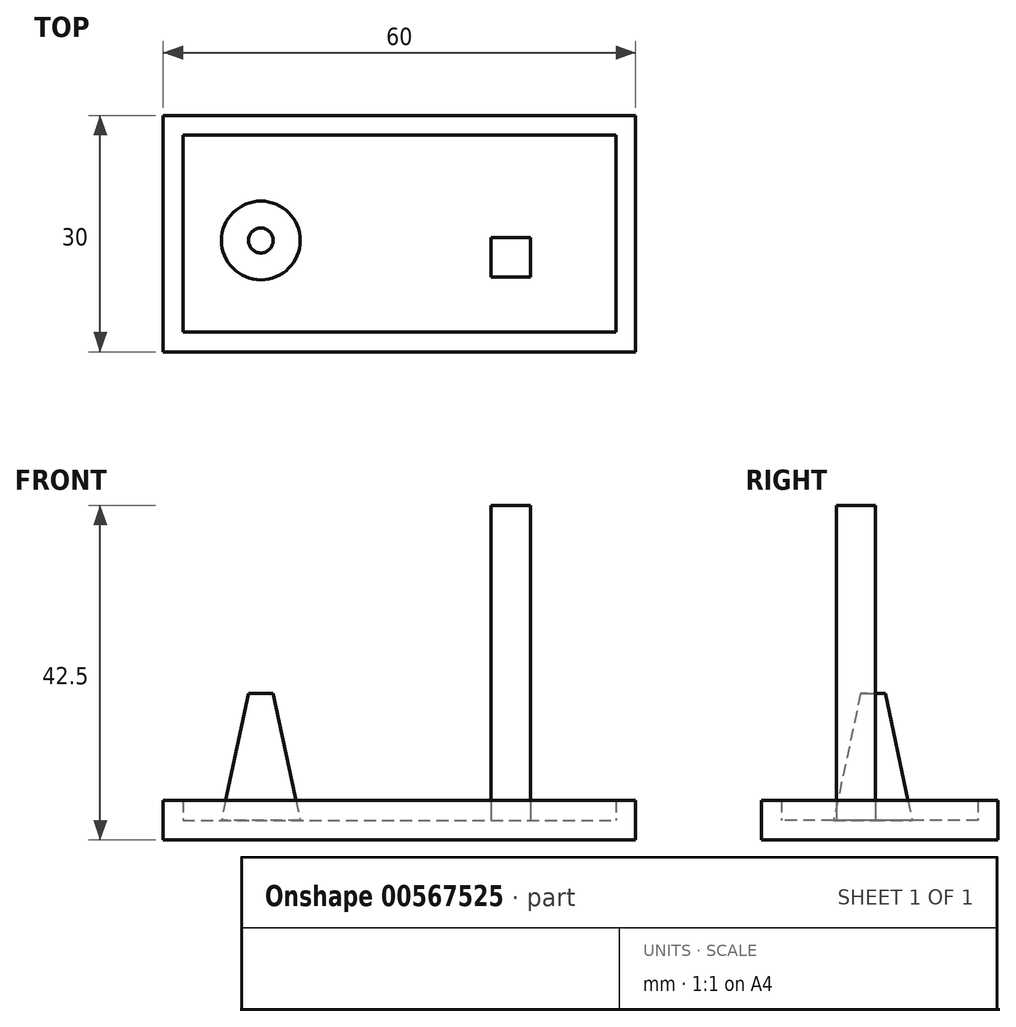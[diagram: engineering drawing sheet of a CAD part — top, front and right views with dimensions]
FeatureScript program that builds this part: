
annotation { "Feature Type Name" : "Feature", "Feature Type Description" : "" }
export const myFeature = defineFeature(function(context is Context, id is Id, definition is map)
    precondition{}
    {
        {
            var Q0;
            Q0=qCreatedBy(makeId("Top.planeOp"),FACE);
            var sketch = newSketch(context, id + "F0", { "sketchPlane" : qUnion([Q0])});
            skLineSegment(sketch, "E0.bottom", {"start": v(-26.67, 19.74) * mm, "end": v(33.33, 19.74) * mm});
            skLineSegment(sketch, "E0.top", {"start": v(-26.67, -10.26) * mm, "end": v(33.33, -10.26) * mm});
            skLineSegment(sketch, "E0.left", {"start": v(-26.67, 19.74) * mm, "end": v(-26.67, -10.26) * mm});
            skLineSegment(sketch, "E0.right", {"start": v(33.33, 19.74) * mm, "end": v(33.33, -10.26) * mm});
            skSolve(sketch);
        }
        {
            var Q0;
            Q0=makeQuery(id+"F0.imprint","IMPRINT",FACE,{"disambiguationData":[TD([[makeQuery(id+"F0.imprint","IMPRINT",EDGE,{"derivedFrom":sQuery(id+"F0.wireOp",EDGE,"E0.bottom")}),-1.0]])]});
            extrude(context, id + "F1", {"entities" : qUnion([Q0]), "depth" : 5 * mm, "offsetDistance" : 25 * mm});
        }
        {
            var Q0;
            Q0=makeQuery(id+"F1.opExtrude","CAP_FACE",FACE,{"disambiguationData":[OSD([sQuery(id+"F0.wireOp",EDGE,"E0.bottom"),sQuery(id+"F0.wireOp",EDGE,"E0.top"),sQuery(id+"F0.wireOp",EDGE,"E0.left"),sQuery(id+"F0.wireOp",EDGE,"E0.right")])],"isStart":false});
            shell(context, id + "F2", {"entities" : qUnion([Q0]), "thickness" : 2.5 * mm});
        }
        {
            var Q0;
            Q0=qCreatedBy(makeId("Top.planeOp"),FACE);
            var sketch = newSketch(context, id + "F3", { "sketchPlane" : qUnion([Q0])});
            skCircle(sketch, "E1", {"center": v(22.63, 1.18) * mm, "radius": 5 * mm});
            skSolve(sketch);
        }
        {
            var Q0;
            Q0=makeQuery(id+"F3.imprint","IMPRINT",FACE,{"disambiguationData":[TD([[makeQuery(id+"F3.imprint","IMPRINT",EDGE,{"derivedFrom":sQuery(id+"F3.wireOp",EDGE,"E1")}),1.0]])]});
            extrude(context, id + "F4", {"entities" : qUnion([Q0]), "depth" : 16.1 * mm, "offsetDistance" : 25 * mm, "hasDraft" : true, "draftAngle" : 12 * degree, "draftPullDirection" : true});
        }
        {
            var Q0;
            Q0=makeQuery(id+"F4.opExtrude","SWEPT_BODY",BODY,{"disambiguationData":[OSD([sQuery(id+"F3.wireOp",EDGE,"E1")])]});
            transform(context, id + "F5", {"entities" : qUnion([Q0]), "transformType" : TransformType.TRANSLATION_3D, "dx" : -37 * mm, "dy" : 2.7 * mm, "dz" : 5.7 * mm, "makeCopy" : false});
        }
        {
            var Q0;
            Q0=makeQuery(id+"F4.opExtrude","SWEPT_BODY",BODY,{"disambiguationData":[OSD([sQuery(id+"F3.wireOp",EDGE,"E1")])]});
            transform(context, id + "F6", {"entities" : qUnion([Q0]), "transformType" : TransformType.TRANSLATION_3D, "dx" : 0.1 * mm, "dy" : 0 * mm, "dz" : -3.2 * mm, "makeCopy" : false});
        }
        {
            var Q0;
            Q0=makeQuery(id+"F2.opShell","OFFSET_FACE",FACE,{"disambiguationData":[OSD([sQuery(id+"F0.wireOp",EDGE,"E0.bottom"),sQuery(id+"F0.wireOp",EDGE,"E0.top"),sQuery(id+"F0.wireOp",EDGE,"E0.left"),sQuery(id+"F0.wireOp",EDGE,"E0.right")])]});
            var sketch = newSketch(context, id + "F7", { "sketchPlane" : qUnion([Q0])});
            skLineSegment(sketch, "E2.bottom", {"start": v(14.97, 4.24) * mm, "end": v(19.97, 4.24) * mm});
            skLineSegment(sketch, "E2.top", {"start": v(14.97, -0.76) * mm, "end": v(19.97, -0.76) * mm});
            skLineSegment(sketch, "E2.left", {"start": v(14.97, 4.24) * mm, "end": v(14.97, -0.76) * mm});
            skLineSegment(sketch, "E2.right", {"start": v(19.97, 4.24) * mm, "end": v(19.97, -0.76) * mm});
            skSolve(sketch);
        }
        {
            var Q0;
            Q0=makeQuery(id+"F7.imprint","IMPRINT",FACE,{"disambiguationData":[TD([[makeQuery(id+"F7.imprint","IMPRINT",EDGE,{"derivedFrom":sQuery(id+"F7.wireOp",EDGE,"E2.bottom")}),-1.0]])]});
            extrude(context, id + "F8", {"entities" : qUnion([Q0]), "operationType" : NewBodyOperationType.ADD, "depth" : 40 * mm, "offsetDistance" : 25 * mm});
        }
    });
